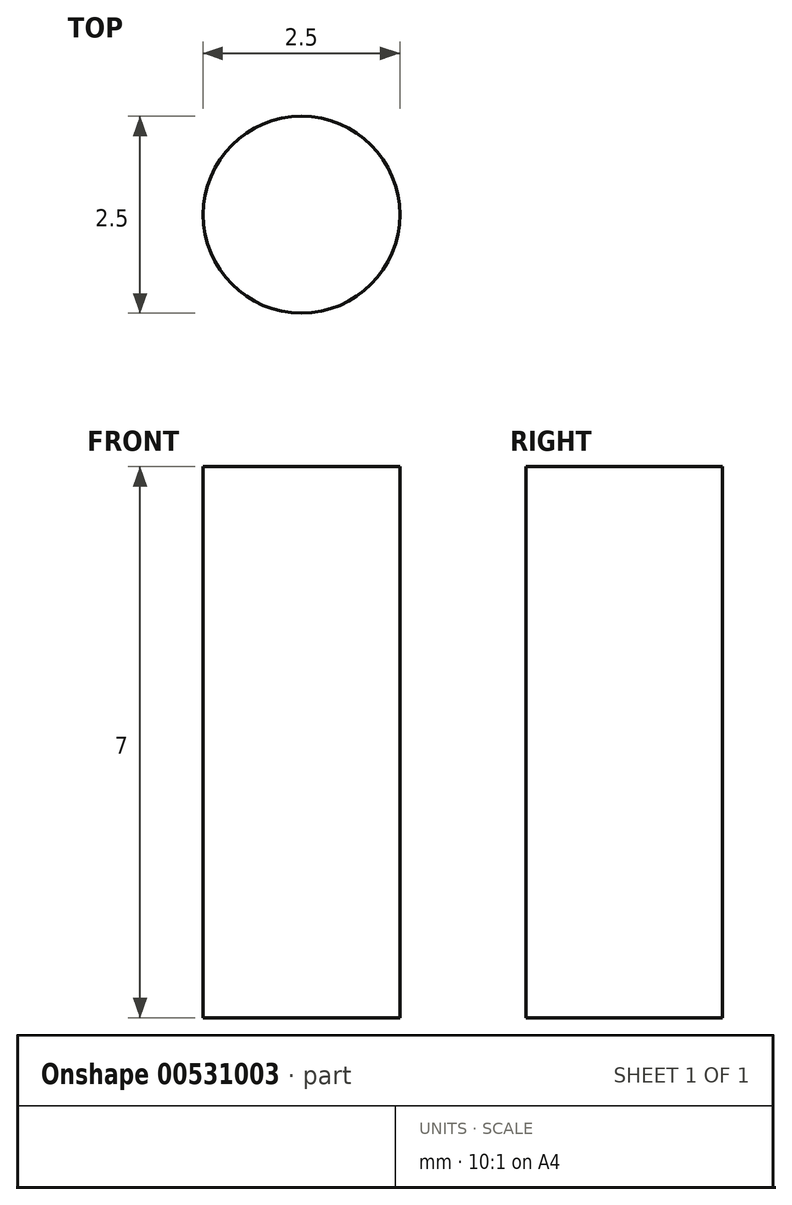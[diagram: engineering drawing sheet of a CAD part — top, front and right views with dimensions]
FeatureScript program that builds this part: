
annotation { "Feature Type Name" : "Feature", "Feature Type Description" : "" }
export const myFeature = defineFeature(function(context is Context, id is Id, definition is map)
    precondition{}
    {
        {
            var Q0;
            Q0=qCreatedBy(makeId("Top.planeOp"),FACE);
            var sketch = newSketch(context, id + "F0", { "sketchPlane" : qUnion([Q0])});
            skCircle(sketch, "E0", {"center": v(0, 0) * mm, "radius": 1.25 * mm});
            skSolve(sketch);
        }
        {
            var Q0;
            Q0 = qSketchRegion(id + "F0", true);
            extrude(context, id + "F1", {"entities" : qUnion([Q0]), "depth" : 7 * mm, "offsetDistance" : 25 * mm});
        }
    });
